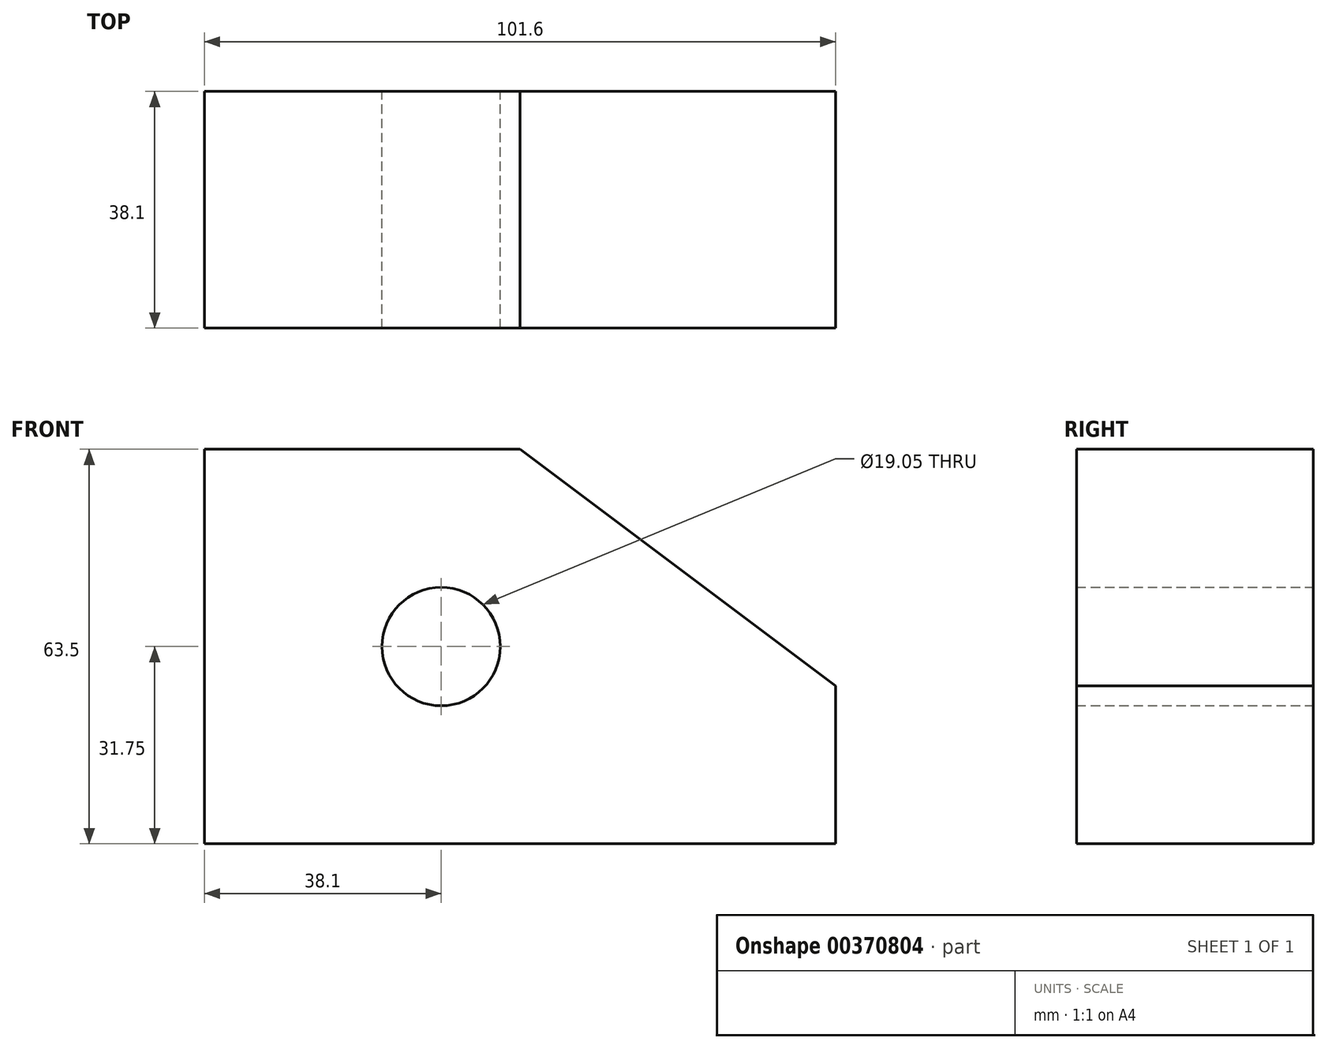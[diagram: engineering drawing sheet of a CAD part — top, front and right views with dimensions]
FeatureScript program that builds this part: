
annotation { "Feature Type Name" : "Feature", "Feature Type Description" : "" }
export const myFeature = defineFeature(function(context is Context, id is Id, definition is map)
    precondition{}
    {
        {
            var Q0;
            Q0=qCreatedBy(makeId("Front.planeOp"),FACE);
            var sketch = newSketch(context, id + "F0", { "sketchPlane" : qUnion([Q0])});
            skLineSegment(sketch, "E0", {"start": v(0, 0) * mm, "end": v(50.8, 0) * mm});
            skLineSegment(sketch, "E1", {"start": v(50.8, 0) * mm, "end": v(101.6, -38.1) * mm});
            skLineSegment(sketch, "E2", {"start": v(101.6, -38.1) * mm, "end": v(101.6, -63.5) * mm});
            skLineSegment(sketch, "E3", {"start": v(101.6, -63.5) * mm, "end": v(0, -63.5) * mm});
            skLineSegment(sketch, "E4", {"start": v(0, -63.5) * mm, "end": v(0, 0) * mm});
            skCircle(sketch, "E5", {"center": v(38.1, -31.75) * mm, "radius": 9.53 * mm});
            skSolve(sketch);
        }
        {
            var Q0;
            Q0=makeQuery(id+"F0.imprint","IMPRINT",FACE,{"disambiguationData":[TD([[makeQuery(id+"F0.imprint","IMPRINT",EDGE,{"derivedFrom":sQuery(id+"F0.wireOp",EDGE,"E0")}),-1.0]])]});
            extrude(context, id + "F1", {"entities" : qUnion([Q0]), "depth" : 38.1 * mm});
        }
    });
